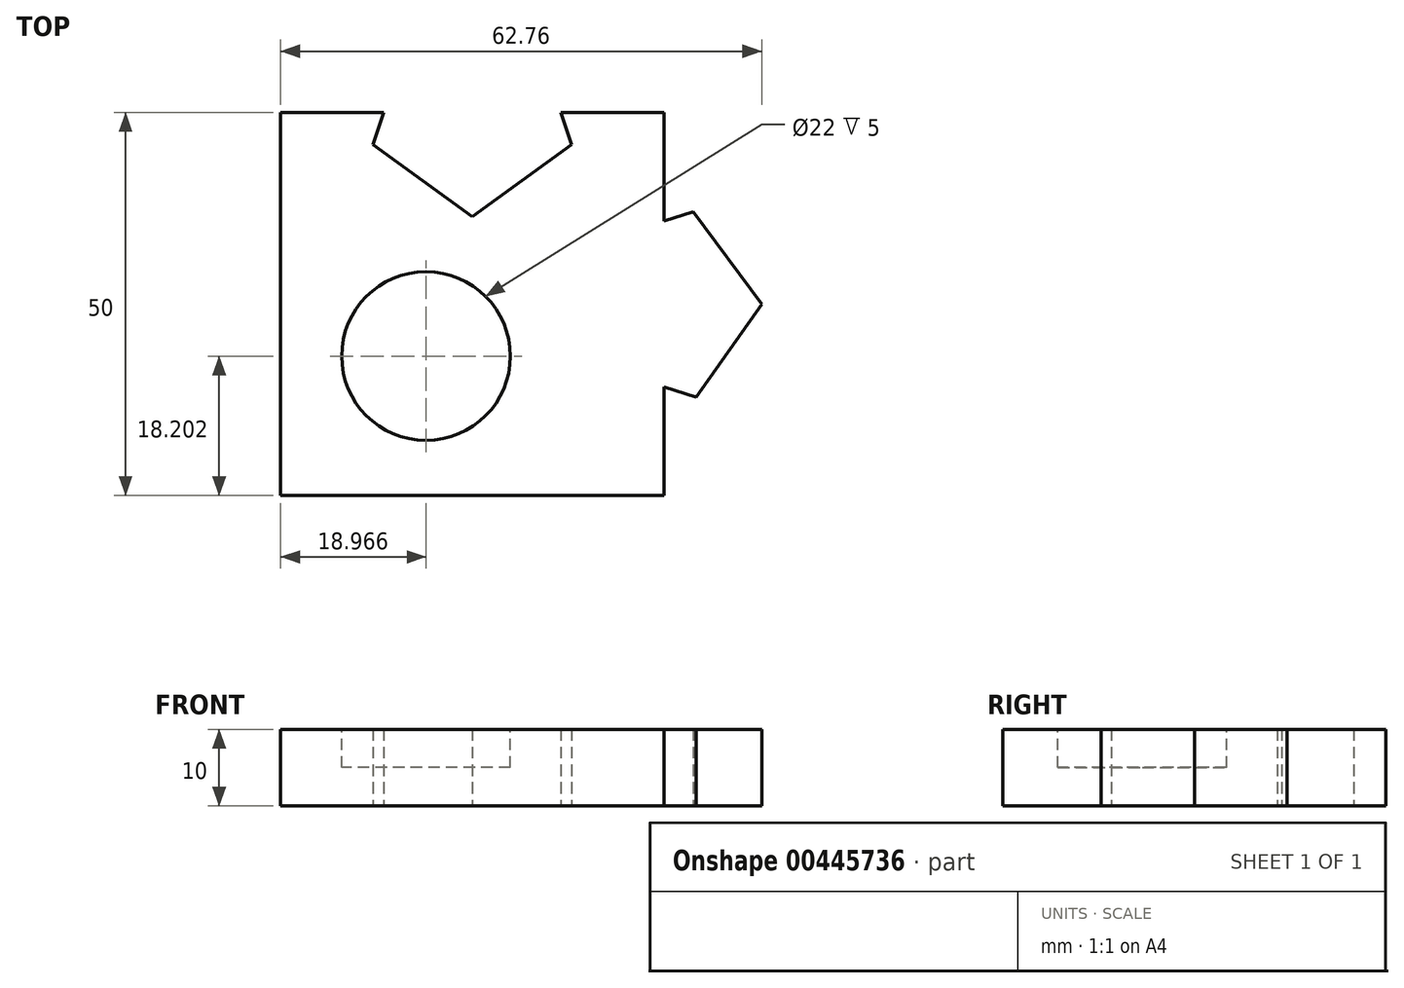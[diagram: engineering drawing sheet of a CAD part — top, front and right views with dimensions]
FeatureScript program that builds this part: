
annotation { "Feature Type Name" : "Feature", "Feature Type Description" : "" }
export const myFeature = defineFeature(function(context is Context, id is Id, definition is map)
    precondition{}
    {
        {
            var Q0;
            Q0=qCreatedBy(makeId("Top.planeOp"),FACE);
            var sketch = newSketch(context, id + "F0", { "sketchPlane" : qUnion([Q0])});
            skLineSegment(sketch, "E0.bottom", {"start": v(25, -25) * mm, "end": v(-25, -25) * mm});
            skLineSegment(sketch, "E0.top", {"start": v(25, 25) * mm, "end": v(-25, 25) * mm});
            skLineSegment(sketch, "E0.left", {"start": v(25, -25) * mm, "end": v(25, 25) * mm});
            skLineSegment(sketch, "E0.right", {"start": v(-25, -25) * mm, "end": v(-25, 25) * mm});
            skPoint(sketch, "E0.middle", {"position": v(0, 0) * mm});
            skLineSegment(sketch, "E1", {"start": v(25, 25) * mm, "end": v(15, 25) * mm, "construction": true});
            skLineSegment(sketch, "E2", {"start": v(15, 25) * mm, "end": v(15, -25) * mm, "construction": true});
            skCircle(sketch, "E3.cCircle", {"center": v(25, 0) * mm, "radius": 10 * mm, "construction": true});
            skLineSegment(sketch, "E3.0", {"start": v(15, -7.27) * mm, "end": v(15, 7.27) * mm});
            skLineSegment(sketch, "E3.1", {"start": v(15, 7.27) * mm, "end": v(28.82, 11.76) * mm});
            skLineSegment(sketch, "E3.2", {"start": v(28.82, 11.76) * mm, "end": v(37.36, 0) * mm});
            skLineSegment(sketch, "E3.3", {"start": v(37.36, 0) * mm, "end": v(28.82, -11.76) * mm});
            skLineSegment(sketch, "E3.4", {"start": v(28.82, -11.76) * mm, "end": v(15, -7.27) * mm});
            skPoint(sketch, "E3.0.midPoint", {"position": v(15, 0) * mm});
            skLineSegment(sketch, "E4", {"start": v(-25, 25) * mm, "end": v(-25, 36) * mm, "construction": true});
            skLineSegment(sketch, "E5", {"start": v(-25, 36) * mm, "end": v(25, 36) * mm, "construction": true});
            skCircle(sketch, "E6.cCircle", {"center": v(0, 25) * mm, "radius": 11 * mm, "construction": true});
            skLineSegment(sketch, "E6.0", {"start": v(-8, 36) * mm, "end": v(8, 36) * mm});
            skLineSegment(sketch, "E6.1", {"start": v(8, 36) * mm, "end": v(12.93, 20.8) * mm});
            skLineSegment(sketch, "E6.2", {"start": v(12.93, 20.8) * mm, "end": v(0, 11.4) * mm});
            skLineSegment(sketch, "E6.3", {"start": v(0, 11.4) * mm, "end": v(-12.93, 20.8) * mm});
            skLineSegment(sketch, "E6.4", {"start": v(-12.93, 20.8) * mm, "end": v(-8, 36) * mm});
            skPoint(sketch, "E6.0.midPoint", {"position": v(0, 36) * mm});
            skLineSegment(sketch, "E7", {"start": v(28.82, 11.76) * mm, "end": v(28.82, 12.06) * mm, "construction": true});
            skLineSegment(sketch, "E8", {"start": v(15, 7.27) * mm, "end": v(15, 8.47) * mm, "construction": true});
            skLineSegment(sketch, "E9", {"start": v(25, 10.51) * mm, "end": v(25, 10.81) * mm, "construction": true});
            skLineSegment(sketch, "E10", {"start": v(25, 10.81) * mm, "end": v(28.82, 12.06) * mm});
            skLineSegment(sketch, "E11", {"start": v(25, 0) * mm, "end": v(37.36, 0) * mm, "construction": true});
            skLineSegment(sketch, "E12.MirrorCS", {"start": v(25, -10.81) * mm, "end": v(28.82, -12.06) * mm});
            skLineSegment(sketch, "E13", {"start": v(37.36, 0) * mm, "end": v(37.76, 0) * mm});
            skLineSegment(sketch, "E14", {"start": v(28.82, 12.06) * mm, "end": v(37.76, 0) * mm});
            skLineSegment(sketch, "E15", {"start": v(28.82, -12.06) * mm, "end": v(29.2, -12.18) * mm});
            skLineSegment(sketch, "E16.MirrorCS", {"start": v(28.82, 12.06) * mm, "end": v(29.2, 12.18) * mm});
            skLineSegment(sketch, "E17", {"start": v(29.2, 12.18) * mm, "end": v(37.76, 0) * mm});
            skLineSegment(sketch, "E18", {"start": v(29.2, -12.18) * mm, "end": v(37.76, 0) * mm});
            skSolve(sketch);
        }
        {
            var Q0;
            {var subQ10=sQuery(id+"F0.wireOp",EDGE,"E0.bottom");Q0=makeQuery(id+"F0.imprint","IMPRINT",FACE,{"disambiguationData":[TD([[makeQuery(id+"F0.imprint","IMPRINT",EDGE,{"derivedFrom":subQ10}),-1.0]])]});}
            var Q1;
            {var subQ1=sQuery(id+"F0.wireOp",EDGE,"E3.2");Q1=makeQuery(id+"F0.imprint","IMPRINT",FACE,{"disambiguationData":[TD([[makeQuery(id+"F0.imprint","IMPRINT",EDGE,{"derivedFrom":subQ1}),-1.0]])]});}
            var Q2;
            {var subQ5=sQuery(id+"F0.wireOp",EDGE,"E3.0");Q2=makeQuery(id+"F0.imprint","IMPRINT",FACE,{"disambiguationData":[TD([[makeQuery(id+"F0.imprint","IMPRINT",EDGE,{"derivedFrom":subQ5}),-1.0]])]});}
            var Q3;
            {var subQ1=sQuery(id+"F0.wireOp",EDGE,"E3.2");Q3=makeQuery(id+"F0.imprint","IMPRINT",FACE,{"disambiguationData":[TD([[makeQuery(id+"F0.imprint","IMPRINT",EDGE,{"derivedFrom":subQ1}),1.0]])]});}
            var Q4;
            {var subQ0=sQuery(id+"F0.wireOp",EDGE,"QyKV0rG1-vVza-FIkl-y8fn-GdQeqrRuVtXp");var subQ1=sQuery(id+"F0.wireOp",EDGE,"E0.left");var subQ2=makeQuery(id+"F0.imprint","INTERSECT",VERTEX,{"derivedFrom":[subQ1,subQ0]});Q4=makeQuery(id+"F0.imprint","IMPRINT",FACE,{"disambiguationData":[TD([[makeQuery(id+"F0.imprint","IMPRINT",EDGE,{"disambiguationData":[TD([[subQ2,1.0]])],"derivedFrom":subQ1}),1.0]])]});}
            var Q5;
            {var subQ2=sQuery(id+"F0.wireOp",EDGE,"E3.3");Q5=makeQuery(id+"F0.imprint","IMPRINT",FACE,{"disambiguationData":[TD([[makeQuery(id+"F0.imprint","IMPRINT",EDGE,{"derivedFrom":subQ2}),1.0]])]});}
            extrude(context, id + "F1", {"entities" : qUnion([Q0, Q1, Q2, Q3, Q4, Q5]), "depth" : 10 * mm});
        }
        {
            var Q0;
            Q0=makeQuery(id+"F1.opExtrude","CAP_FACE",FACE,{"disambiguationData":[OSD([sQuery(id+"F0.wireOp",EDGE,"E0.bottom"),sQuery(id+"F0.wireOp",EDGE,"E0.top"),sQuery(id+"F0.wireOp",EDGE,"E0.left"),sQuery(id+"F0.wireOp",EDGE,"E0.right"),sQuery(id+"F0.wireOp",EDGE,"E3.1"),sQuery(id+"F0.wireOp",EDGE,"E3.2"),sQuery(id+"F0.wireOp",EDGE,"E3.3"),sQuery(id+"F0.wireOp",EDGE,"E3.4"),sQuery(id+"F0.wireOp",EDGE,"E6.1"),sQuery(id+"F0.wireOp",EDGE,"E6.2"),sQuery(id+"F0.wireOp",EDGE,"E6.3"),sQuery(id+"F0.wireOp",EDGE,"E6.4")])],"isStart":false});
            var sketch = newSketch(context, id + "F2", { "sketchPlane" : qUnion([Q0])});
            skLineSegment(sketch, "E19", {"start": v(-25, 11.4) * mm, "end": v(25, 11.4) * mm, "construction": true});
            skLineSegment(sketch, "E20", {"start": v(12.93, 25) * mm, "end": v(12.93, -25) * mm, "construction": true});
            skLineSegment(sketch, "E21", {"start": v(-25, 11.4) * mm, "end": v(12.93, -25) * mm, "construction": true});
            skCircle(sketch, "E22", {"center": v(-6.03, -6.8) * mm, "radius": 11 * mm});
            skSolve(sketch);
        }
        {
            var Q0;
            Q0=makeQuery(id+"F2.imprint","IMPRINT",FACE,{"disambiguationData":[TD([[makeQuery(id+"F2.imprint","IMPRINT",EDGE,{"derivedFrom":sQuery(id+"F2.wireOp",EDGE,"E22")}),1.0]])]});
            extrude(context, id + "F3", {"entities" : qUnion([Q0]), "operationType" : NewBodyOperationType.REMOVE, "oppositeDirection" : true, "depth" : 5 * mm});
        }
    });
